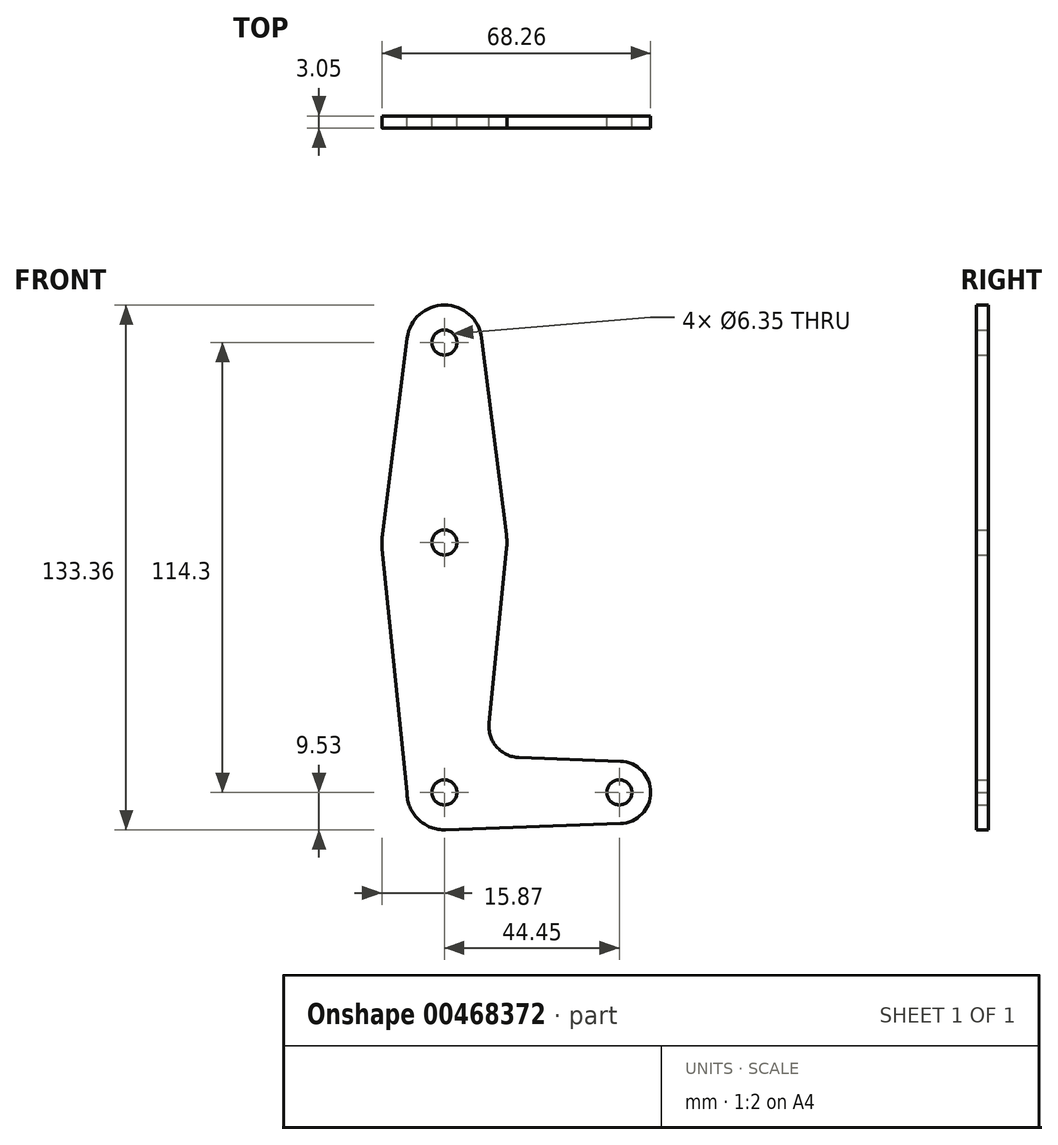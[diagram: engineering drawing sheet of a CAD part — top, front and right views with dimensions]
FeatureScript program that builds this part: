
annotation { "Feature Type Name" : "Feature", "Feature Type Description" : "" }
export const myFeature = defineFeature(function(context is Context, id is Id, definition is map)
    precondition{}
    {
        {
            var Q0;
            Q0=qCreatedBy(makeId("Front.planeOp"),FACE);
            var sketch = newSketch(context, id + "F0", { "sketchPlane" : qUnion([Q0])});
            skLineSegment(sketch, "E0", {"start": v(0, 114.3) * mm, "end": v(0, 0) * mm, "construction": true});
            skLineSegment(sketch, "E1", {"start": v(0, 0) * mm, "end": v(44.45, 0) * mm, "construction": true});
            skCircle(sketch, "E2", {"center": v(0, 114.3) * mm, "radius": 9.53 * mm});
            skCircle(sketch, "E3", {"center": v(0, 63.5) * mm, "radius": 15.88 * mm});
            skCircle(sketch, "E4", {"center": v(0, 0) * mm, "radius": 9.53 * mm});
            skCircle(sketch, "E5", {"center": v(44.45, 0) * mm, "radius": 7.94 * mm});
            skLineSegment(sketch, "E6", {"start": v(9.45, 115.5) * mm, "end": v(15.75, 65.48) * mm});
            skLineSegment(sketch, "E7", {"start": v(0.34, -9.52) * mm, "end": v(44.73, -7.93) * mm});
            skLineSegment(sketch, "E8", {"start": v(-9.45, 115.5) * mm, "end": v(-15.75, 65.48) * mm});
            skCircle(sketch, "E9", {"center": v(0, 114.3) * mm, "radius": 3.18 * mm});
            skCircle(sketch, "E10", {"center": v(0, 63.5) * mm, "radius": 3.18 * mm});
            skCircle(sketch, "E11", {"center": v(44.45, 0) * mm, "radius": 3.18 * mm});
            skCircle(sketch, "E12", {"center": v(-3.17, 100.03) * mm, "radius": 3.18 * mm});
            skLineSegment(sketch, "E13", {"start": v(15.8, 61.91) * mm, "end": v(11.34, 17.6) * mm});
            skLineSegment(sketch, "E14", {"start": v(18.97, 8.85) * mm, "end": v(44.73, 7.93) * mm});
            skArc(sketch, "E15.filletArc", {"start": v(11.34, 17.6) * mm, "mid": v(13.26, 11.57) * mm, "end": v(18.97, 8.85) * mm});
            skCircle(sketch, "E16", {"center": v(0, 0) * mm, "radius": 3.18 * mm});
            skLineSegment(sketch, "E17", {"start": v(-15.8, 61.9) * mm, "end": v(-9.52, 0) * mm});
            skSolve(sketch);
        }
        {
            var Q0;
            Q0=makeQuery(id+"F0.imprint","IMPRINT",FACE,{"disambiguationData":[TD([[makeQuery(id+"F0.imprint","IMPRINT",EDGE,{"derivedFrom":sQuery(id+"F0.wireOp",EDGE,"E9")}),-1.0]])]});
            var Q1;
            Q1=makeQuery(id+"F0.imprint","IMPRINT",FACE,{"disambiguationData":[TD([[makeQuery(id+"F0.imprint","IMPRINT",EDGE,{"derivedFrom":sQuery(id+"F0.wireOp",EDGE,"E12")}),1.0]])]});
            var Q2;
            Q2=makeQuery(id+"F0.imprint","IMPRINT",FACE,{"disambiguationData":[TD([[makeQuery(id+"F0.imprint","IMPRINT",EDGE,{"derivedFrom":sQuery(id+"F0.wireOp",EDGE,"E10")}),-1.0]])]});
            var Q3;
            {var subQ0=sQuery(id+"F0.wireOp",EDGE,"E6");Q3=makeQuery(id+"F0.imprint","IMPRINT",FACE,{"disambiguationData":[TD([[makeQuery(id+"F0.imprint","IMPRINT",EDGE,{"derivedFrom":subQ0}),-1.0]])]});}
            var Q4;
            {var subQ0=sQuery(id+"F0.wireOp",EDGE,"E7");Q4=makeQuery(id+"F0.imprint","IMPRINT",FACE,{"disambiguationData":[TD([[makeQuery(id+"F0.imprint","IMPRINT",EDGE,{"derivedFrom":subQ0}),1.0]])]});}
            var Q5;
            Q5=makeQuery(id+"F0.imprint","IMPRINT",FACE,{"disambiguationData":[TD([[makeQuery(id+"F0.imprint","IMPRINT",EDGE,{"derivedFrom":sQuery(id+"F0.wireOp",EDGE,"E16")}),-1.0]])]});
            var Q6;
            Q6=makeQuery(id+"F0.imprint","IMPRINT",FACE,{"disambiguationData":[TD([[makeQuery(id+"F0.imprint","IMPRINT",EDGE,{"derivedFrom":sQuery(id+"F0.wireOp",EDGE,"E11")}),-1.0]])]});
            extrude(context, id + "F1", {"entities" : qUnion([Q0, Q1, Q2, Q3, Q4, Q5, Q6]), "depth" : 3.05 * mm});
        }
    });
